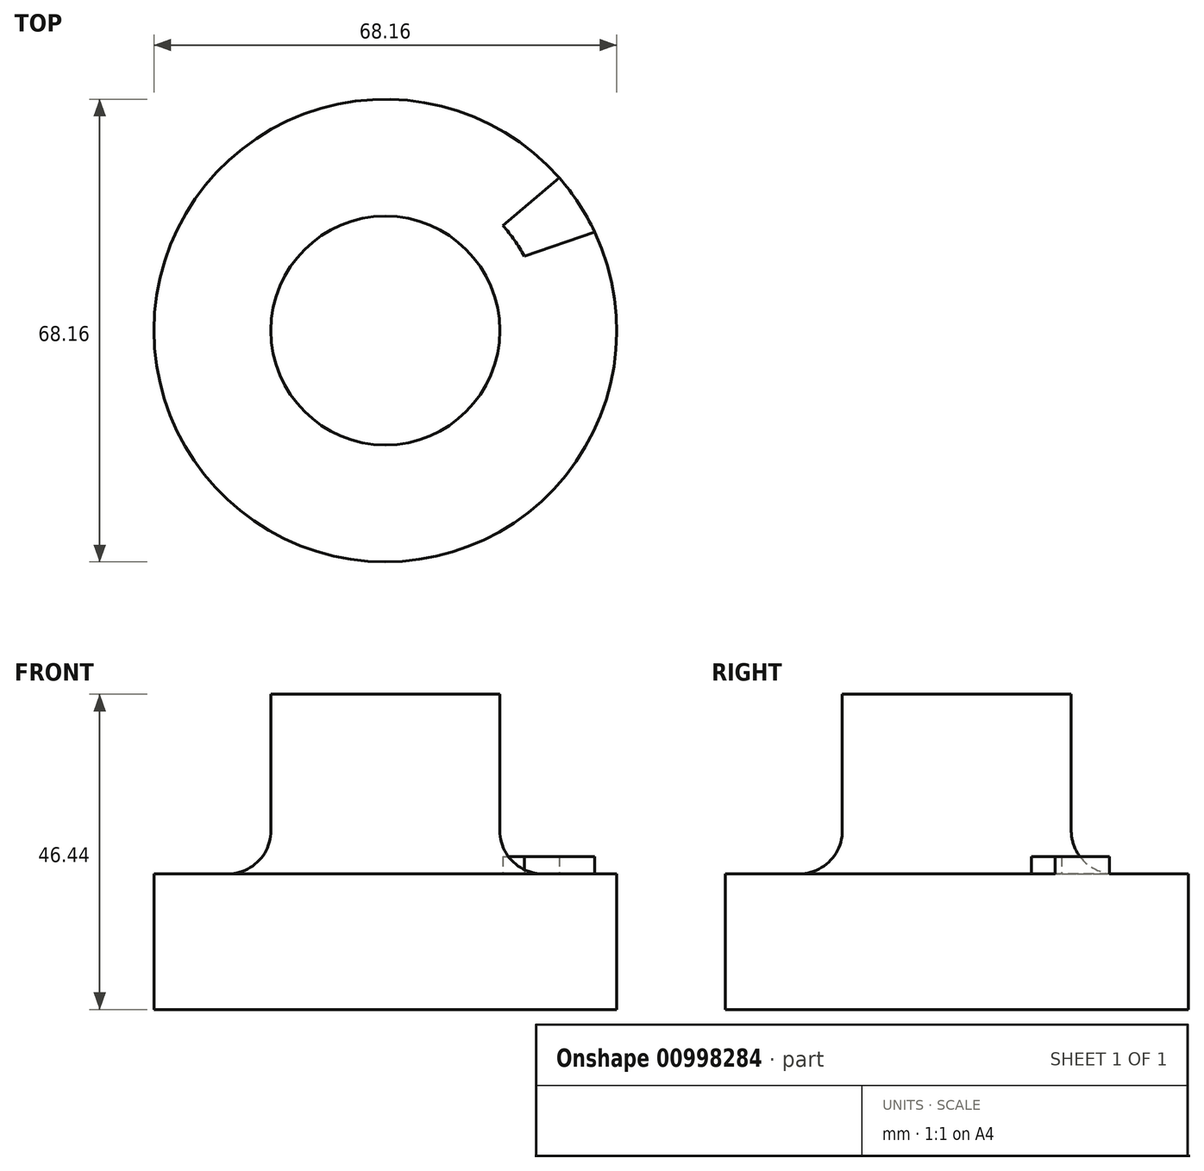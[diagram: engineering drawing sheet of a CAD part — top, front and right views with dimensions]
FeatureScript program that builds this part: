
annotation { "Feature Type Name" : "Feature", "Feature Type Description" : "" }
export const myFeature = defineFeature(function(context is Context, id is Id, definition is map)
    precondition{}
    {
        {
            var Q0;
            Q0=qCreatedBy(makeId("Front.planeOp"),FACE);
            var sketch = newSketch(context, id + "F0", { "sketchPlane" : qUnion([Q0])});
            skLineSegment(sketch, "E0.bottom", {"start": v(0, 0) * mm, "end": v(-34.08, 0) * mm});
            skLineSegment(sketch, "E0.left", {"start": v(0, 0) * mm, "end": v(0, 19.99) * mm});
            skLineSegment(sketch, "E0.right", {"start": v(-34.08, 0) * mm, "end": v(-34.08, 19.99) * mm});
            skLineSegment(sketch, "E1", {"start": v(0, 0) * mm, "end": v(0, 46.44) * mm});
            skLineSegment(sketch, "E2", {"start": v(0, 46.44) * mm, "end": v(-16.86, 46.44) * mm});
            skLineSegment(sketch, "E3", {"start": v(-16.86, 46.44) * mm, "end": v(-16.86, 26.34) * mm});
            skLineSegment(sketch, "E4", {"start": v(-23.2, 19.99) * mm, "end": v(-34.08, 19.99) * mm});
            skPoint(sketch, "E5.visualSharp", {"position": v(-16.86, 19.99) * mm});
            skArc(sketch, "E5.filletArc", {"start": v(-23.2, 19.99) * mm, "mid": v(-18.72, 21.85) * mm, "end": v(-16.86, 26.34) * mm});
            skSolve(sketch);
        }
        {
            var Q0;
            {var subQ2=sQuery(id+"F0.wireOp",EDGE,"E0.bottom");Q0=makeQuery(id+"F0.imprint","IMPRINT",FACE,{"disambiguationData":[TD([[makeQuery(id+"F0.imprint","IMPRINT",EDGE,{"derivedFrom":subQ2}),-1.0]])]});}
            var Q1;
            Q1=sQuery(id+"F0.wireOp",EDGE,"E1");
            revolve(context, id + "F1", {"surfaceOperationType" : NewSurfaceOperationType.NEW, "entities" : qUnion([Q0]), "axis" : qUnion([Q1]), "revolveType" : RevolveType.FULL});
        }
        {
            var Q0;
            Q0=makeQuery(id+"F1.opRevolve","SWEPT_FACE",FACE,{"disambiguationData":[OSD([sQuery(id+"F0.wireOp",EDGE,"E4")])]});
            var sketch = newSketch(context, id + "F2", { "sketchPlane" : qUnion([Q0])});
            skLineSegment(sketch, "E6", {"start": v(17.32, 15.45) * mm, "end": v(25.6, 22.5) * mm});
            skLineSegment(sketch, "E7", {"start": v(30.84, 14.51) * mm, "end": v(20.45, 10.97) * mm});
            skSolve(sketch);
        }
        {
            var Q0;
            {var subQ0=sQuery(id+"F2.wireOp",EDGE,"E6");Q0=makeQuery(id+"F2.imprint","IMPRINT",FACE,{"disambiguationData":[TD([[makeQuery(id+"F2.imprint","IMPRINT",EDGE,{"derivedFrom":subQ0}),-1.0]])]});}
            extrude(context, id + "F3", {"entities" : qUnion([Q0]), "operationType" : NewBodyOperationType.ADD, "depth" : 2.54 * mm, "offsetDistance" : 25.4 * mm});
        }
    });
